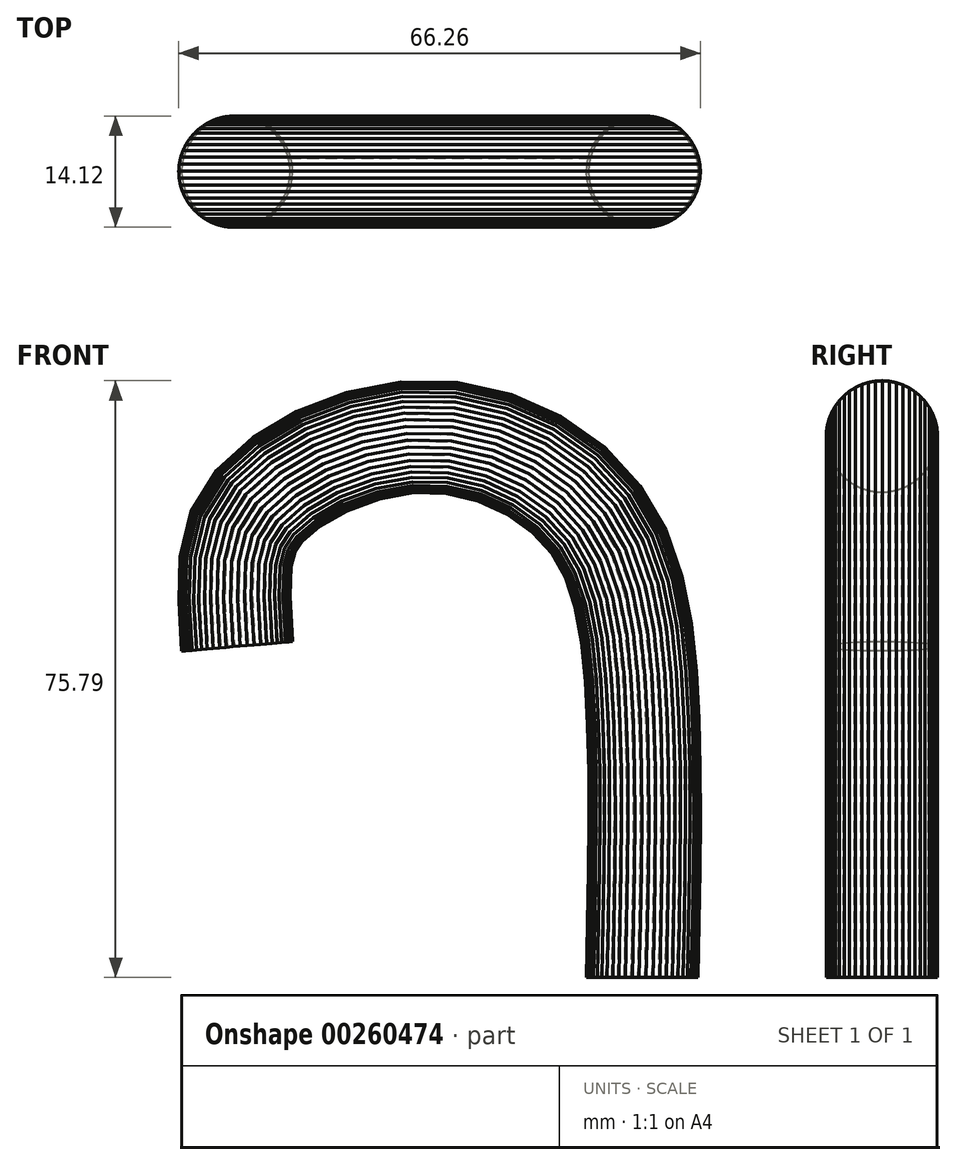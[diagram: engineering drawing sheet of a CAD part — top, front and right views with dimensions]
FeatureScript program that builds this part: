
annotation { "Feature Type Name" : "Feature", "Feature Type Description" : "" }
export const myFeature = defineFeature(function(context is Context, id is Id, definition is map)
    precondition{}
    {
        {
            var Q0;
            Q0=qCreatedBy(makeId("Front.planeOp"),FACE);
            var sketch = newSketch(context, id + "F0", { "sketchPlane" : qUnion([Q0])});
            skFitSpline(sketch, "E0", {"points": [v(0, 0) * mm, v(0, 35.65) * mm, v(-6.07, 58.4) * mm, v(-27.6, 68.72) * mm, v(-48.85, 59.62) * mm, v(-51.43, 42.06) * mm], "startDerivative": vector(3.59, 160.9) * mm, "endDerivative": vector(10.22, -157.27) * mm});
            skSolve(sketch);
        }
        {
            var Q0;
            Q0=qCreatedBy(makeId("Top.planeOp"),FACE);
            var sketch = newSketch(context, id + "F1", { "sketchPlane" : qUnion([Q0])});
            skCircle(sketch, "E1.cCircle", {"center": v(0, 0) * mm, "radius": 7.06 * mm, "construction": true});
            skLineSegment(sketch, "E1.0", {"start": v(2.95, 6.43) * mm, "end": v(3.73, 6) * mm});
            skLineSegment(sketch, "E1.1", {"start": v(3.73, 6) * mm, "end": v(4.45, 5.5) * mm});
            skLineSegment(sketch, "E1.2", {"start": v(4.45, 5.5) * mm, "end": v(5.1, 4.9) * mm});
            skLineSegment(sketch, "E1.3", {"start": v(5.1, 4.9) * mm, "end": v(5.68, 4.22) * mm});
            skLineSegment(sketch, "E1.4", {"start": v(5.68, 4.22) * mm, "end": v(6.16, 3.47) * mm});
            skLineSegment(sketch, "E1.5", {"start": v(6.16, 3.47) * mm, "end": v(6.55, 2.67) * mm});
            skLineSegment(sketch, "E1.6", {"start": v(6.55, 2.67) * mm, "end": v(6.83, 1.83) * mm});
            skLineSegment(sketch, "E1.7", {"start": v(6.83, 1.83) * mm, "end": v(7, 0.96) * mm});
            skLineSegment(sketch, "E1.8", {"start": v(7, 0.96) * mm, "end": v(7.07, 0.07) * mm});
            skLineSegment(sketch, "E1.9", {"start": v(7.07, 0.07) * mm, "end": v(7.03, -0.82) * mm});
            skLineSegment(sketch, "E1.10", {"start": v(7.03, -0.82) * mm, "end": v(6.87, -1.69) * mm});
            skLineSegment(sketch, "E1.11", {"start": v(6.87, -1.69) * mm, "end": v(6.6, -2.54) * mm});
            skLineSegment(sketch, "E1.12", {"start": v(6.6, -2.54) * mm, "end": v(6.23, -3.34) * mm});
            skLineSegment(sketch, "E1.13", {"start": v(6.23, -3.34) * mm, "end": v(5.76, -4.1) * mm});
            skLineSegment(sketch, "E1.14", {"start": v(5.76, -4.1) * mm, "end": v(5.2, -4.79) * mm});
            skLineSegment(sketch, "E1.15", {"start": v(5.2, -4.79) * mm, "end": v(4.56, -5.4) * mm});
            skLineSegment(sketch, "E1.16", {"start": v(4.56, -5.4) * mm, "end": v(3.85, -5.93) * mm});
            skLineSegment(sketch, "E1.17", {"start": v(3.85, -5.93) * mm, "end": v(3.08, -6.37) * mm});
            skLineSegment(sketch, "E1.18", {"start": v(3.08, -6.37) * mm, "end": v(2.25, -6.7) * mm});
            skLineSegment(sketch, "E1.19", {"start": v(2.25, -6.7) * mm, "end": v(1.4, -6.93) * mm});
            skLineSegment(sketch, "E1.20", {"start": v(1.4, -6.93) * mm, "end": v(0.52, -7.05) * mm});
            skLineSegment(sketch, "E1.21", {"start": v(0.52, -7.05) * mm, "end": v(-0.37, -7.06) * mm});
            skLineSegment(sketch, "E1.22", {"start": v(-0.37, -7.06) * mm, "end": v(-1.25, -6.96) * mm});
            skLineSegment(sketch, "E1.23", {"start": v(-1.25, -6.96) * mm, "end": v(-2.12, -6.75) * mm});
            skLineSegment(sketch, "E1.24", {"start": v(-2.12, -6.75) * mm, "end": v(-2.95, -6.43) * mm});
            skLineSegment(sketch, "E1.25", {"start": v(-2.95, -6.43) * mm, "end": v(-3.73, -6) * mm});
            skLineSegment(sketch, "E1.26", {"start": v(-3.73, -6) * mm, "end": v(-4.45, -5.5) * mm});
            skLineSegment(sketch, "E1.27", {"start": v(-4.45, -5.5) * mm, "end": v(-5.1, -4.9) * mm});
            skLineSegment(sketch, "E1.28", {"start": v(-5.1, -4.9) * mm, "end": v(-5.68, -4.22) * mm});
            skLineSegment(sketch, "E1.29", {"start": v(-5.68, -4.22) * mm, "end": v(-6.16, -3.47) * mm});
            skLineSegment(sketch, "E1.30", {"start": v(-6.16, -3.47) * mm, "end": v(-6.55, -2.67) * mm});
            skLineSegment(sketch, "E1.31", {"start": v(-6.55, -2.67) * mm, "end": v(-6.83, -1.83) * mm});
            skLineSegment(sketch, "E1.32", {"start": v(-6.83, -1.83) * mm, "end": v(-7, -0.96) * mm});
            skLineSegment(sketch, "E1.33", {"start": v(-7, -0.96) * mm, "end": v(-7.07, -0.07) * mm});
            skLineSegment(sketch, "E1.34", {"start": v(-7.07, -0.07) * mm, "end": v(-7.03, 0.82) * mm});
            skLineSegment(sketch, "E1.35", {"start": v(-7.03, 0.82) * mm, "end": v(-6.87, 1.69) * mm});
            skLineSegment(sketch, "E1.36", {"start": v(-6.87, 1.69) * mm, "end": v(-6.6, 2.54) * mm});
            skLineSegment(sketch, "E1.37", {"start": v(-6.6, 2.54) * mm, "end": v(-6.23, 3.34) * mm});
            skLineSegment(sketch, "E1.38", {"start": v(-6.23, 3.34) * mm, "end": v(-5.76, 4.1) * mm});
            skLineSegment(sketch, "E1.39", {"start": v(-5.76, 4.1) * mm, "end": v(-5.2, 4.79) * mm});
            skLineSegment(sketch, "E1.40", {"start": v(-5.2, 4.79) * mm, "end": v(-4.56, 5.4) * mm});
            skLineSegment(sketch, "E1.41", {"start": v(-4.56, 5.4) * mm, "end": v(-3.85, 5.93) * mm});
            skLineSegment(sketch, "E1.42", {"start": v(-3.85, 5.93) * mm, "end": v(-3.08, 6.37) * mm});
            skLineSegment(sketch, "E1.43", {"start": v(-3.08, 6.37) * mm, "end": v(-2.25, 6.7) * mm});
            skLineSegment(sketch, "E1.44", {"start": v(-2.25, 6.7) * mm, "end": v(-1.4, 6.93) * mm});
            skLineSegment(sketch, "E1.45", {"start": v(-1.4, 6.93) * mm, "end": v(-0.52, 7.05) * mm});
            skLineSegment(sketch, "E1.46", {"start": v(-0.52, 7.05) * mm, "end": v(0.37, 7.06) * mm});
            skLineSegment(sketch, "E1.47", {"start": v(0.37, 7.06) * mm, "end": v(1.25, 6.96) * mm});
            skLineSegment(sketch, "E1.48", {"start": v(1.25, 6.96) * mm, "end": v(2.12, 6.75) * mm});
            skLineSegment(sketch, "E1.49", {"start": v(2.12, 6.75) * mm, "end": v(2.95, 6.43) * mm});
            skPoint(sketch, "E1.0.midPoint", {"position": v(3.34, 6.22) * mm});
            skSolve(sketch);
        }
        {
            var Q0;
            Q0=makeQuery(id+"F1.imprint","IMPRINT",FACE,{"disambiguationData":[TD([[makeQuery(id+"F1.imprint","IMPRINT",EDGE,{"derivedFrom":sQuery(id+"F1.wireOp",EDGE,"E1.0")}),-1.0]])]});
            var Q1;
            Q1=sQuery(id+"F0.wireOp",EDGE,"E0");
            sweep(context, id + "F2", {"profiles" : qUnion([Q0]), "path" : qUnion([Q1])});
        }
    });
